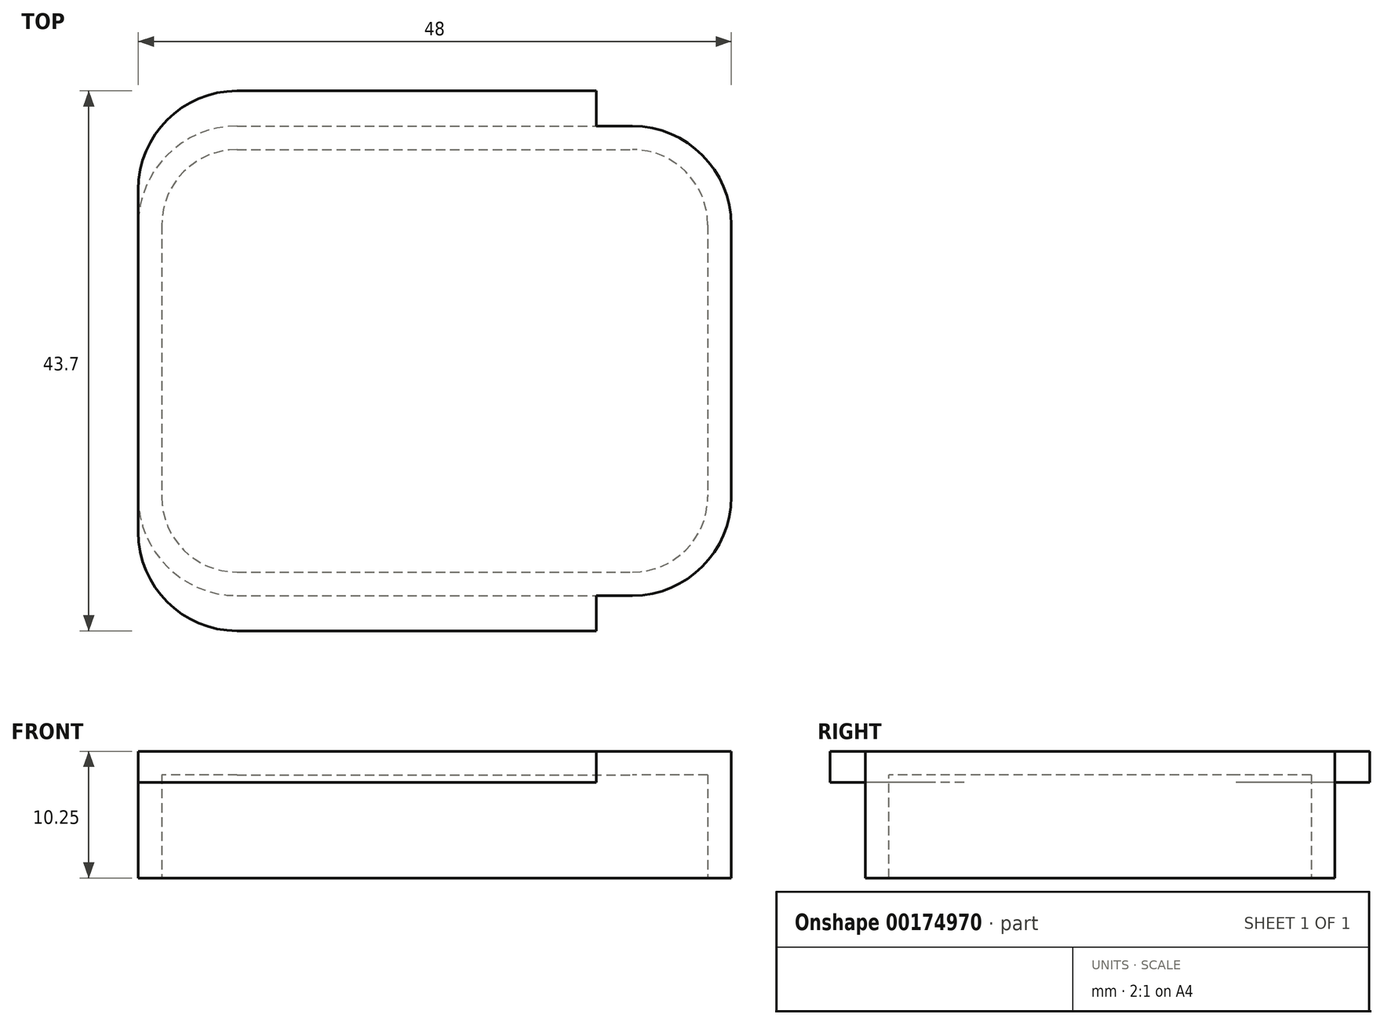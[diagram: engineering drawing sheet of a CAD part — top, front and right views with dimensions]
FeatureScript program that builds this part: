
annotation { "Feature Type Name" : "Feature", "Feature Type Description" : "" }
export const myFeature = defineFeature(function(context is Context, id is Id, definition is map)
    precondition{}
    {
        {
            var Q0;
            Q0=qCreatedBy(makeId("Top.planeOp"),FACE);
            var sketch = newSketch(context, id + "F0", { "sketchPlane" : qUnion([Q0])});
            skLineSegment(sketch, "E0.bottom", {"start": v(-18, 19) * mm, "end": v(14, 19) * mm});
            skLineSegment(sketch, "E0.top", {"start": v(-18, -19) * mm, "end": v(14, -19) * mm});
            skLineSegment(sketch, "E0.left", {"start": v(-26, 11) * mm, "end": v(-26, -11) * mm});
            skLineSegment(sketch, "E0.right", {"start": v(22, 11) * mm, "end": v(22, -11) * mm});
            skPoint(sketch, "E1.visualSharp", {"position": v(-26, 19) * mm});
            skArc(sketch, "E1.filletArc", {"start": v(-18, 19) * mm, "mid": v(-23.66, 16.66) * mm, "end": v(-26, 11) * mm});
            skPoint(sketch, "E2.visualSharp", {"position": v(22, 19) * mm});
            skArc(sketch, "E2.filletArc", {"start": v(22, 11) * mm, "mid": v(19.66, 16.66) * mm, "end": v(14, 19) * mm});
            skPoint(sketch, "E3.visualSharp", {"position": v(22, -19) * mm});
            skArc(sketch, "E3.filletArc", {"start": v(14, -19) * mm, "mid": v(19.66, -16.66) * mm, "end": v(22, -11) * mm});
            skPoint(sketch, "E4.visualSharp", {"position": v(-26, -19) * mm});
            skArc(sketch, "E4.filletArc", {"start": v(-26, -11) * mm, "mid": v(-23.66, -16.66) * mm, "end": v(-18, -19) * mm});
            skSolve(sketch);
        }
        {
            var Q0;
            Q0=makeQuery(id+"F0.imprint","IMPRINT",FACE,{"disambiguationData":[TD([[makeQuery(id+"F0.imprint","IMPRINT",EDGE,{"derivedFrom":sQuery(id+"F0.wireOp",EDGE,"E0.bottom")}),-1.0]])]});
            extrude(context, id + "F1", {"entities" : qUnion([Q0]), "depth" : 10.25 * mm});
        }
        {
            var Q0;
            Q0=makeQuery(id+"F1.opExtrude","CAP_FACE",FACE,{"disambiguationData":[OSD([sQuery(id+"F0.wireOp",EDGE,"E0.bottom"),sQuery(id+"F0.wireOp",EDGE,"E0.top"),sQuery(id+"F0.wireOp",EDGE,"E0.left"),sQuery(id+"F0.wireOp",EDGE,"E0.right"),sQuery(id+"F0.wireOp",EDGE,"E1.filletArc"),sQuery(id+"F0.wireOp",EDGE,"E2.filletArc"),sQuery(id+"F0.wireOp",EDGE,"E3.filletArc"),sQuery(id+"F0.wireOp",EDGE,"E4.filletArc")])],"isStart":false});
            var sketch = newSketch(context, id + "F2", { "sketchPlane" : qUnion([Q0])});
            skLineSegment(sketch, "E5.bottom", {"start": v(-18, 21.85) * mm, "end": v(11.09, 21.85) * mm});
            skLineSegment(sketch, "E5.top", {"start": v(-18, -21.85) * mm, "end": v(11.09, -21.85) * mm});
            skLineSegment(sketch, "E5.left", {"start": v(-26, 13.85) * mm, "end": v(-26, -13.85) * mm});
            skLineSegment(sketch, "E5.right", {"start": v(11.09, 21.85) * mm, "end": v(11.09, -21.85) * mm});
            skPoint(sketch, "E6.visualSharp", {"position": v(-26, 21.85) * mm});
            skArc(sketch, "E6.filletArc", {"start": v(-18, 21.85) * mm, "mid": v(-23.66, 19.5) * mm, "end": v(-26, 13.85) * mm});
            skPoint(sketch, "E7.visualSharp", {"position": v(-26, -21.85) * mm});
            skArc(sketch, "E7.filletArc", {"start": v(-26, -13.85) * mm, "mid": v(-23.66, -19.5) * mm, "end": v(-18, -21.85) * mm});
            skSolve(sketch);
        }
        {
            var Q0;
            Q0 = qSketchRegion(id + "F2", true);
            extrude(context, id + "F3", {"entities" : qUnion([Q0]), "operationType" : NewBodyOperationType.ADD, "oppositeDirection" : true, "depth" : 2.5 * mm});
        }
        {
            var Q0;
            Q0=makeQuery(id+"F1.opExtrude","CAP_FACE",FACE,{"disambiguationData":[OSD([sQuery(id+"F0.wireOp",EDGE,"E0.bottom"),sQuery(id+"F0.wireOp",EDGE,"E0.top"),sQuery(id+"F0.wireOp",EDGE,"E0.left"),sQuery(id+"F0.wireOp",EDGE,"E0.right"),sQuery(id+"F0.wireOp",EDGE,"E1.filletArc"),sQuery(id+"F0.wireOp",EDGE,"E2.filletArc"),sQuery(id+"F0.wireOp",EDGE,"E3.filletArc"),sQuery(id+"F0.wireOp",EDGE,"E4.filletArc")])],"isStart":true});
            var sketch = newSketch(context, id + "F4", { "sketchPlane" : qUnion([Q0])});
            skSolve(sketch);
        }
        {
            var Q0;
            Q0=makeQuery(id+"F1.opExtrude","CAP_FACE",FACE,{"disambiguationData":[OSD([sQuery(id+"F0.wireOp",EDGE,"E0.bottom"),sQuery(id+"F0.wireOp",EDGE,"E0.top"),sQuery(id+"F0.wireOp",EDGE,"E0.left"),sQuery(id+"F0.wireOp",EDGE,"E0.right"),sQuery(id+"F0.wireOp",EDGE,"E1.filletArc"),sQuery(id+"F0.wireOp",EDGE,"E2.filletArc"),sQuery(id+"F0.wireOp",EDGE,"E3.filletArc"),sQuery(id+"F0.wireOp",EDGE,"E4.filletArc")])],"isStart":true});
            shell(context, id + "F5", {"entities" : qUnion([Q0]), "thickness" : 1.9 * mm});
        }
    });
